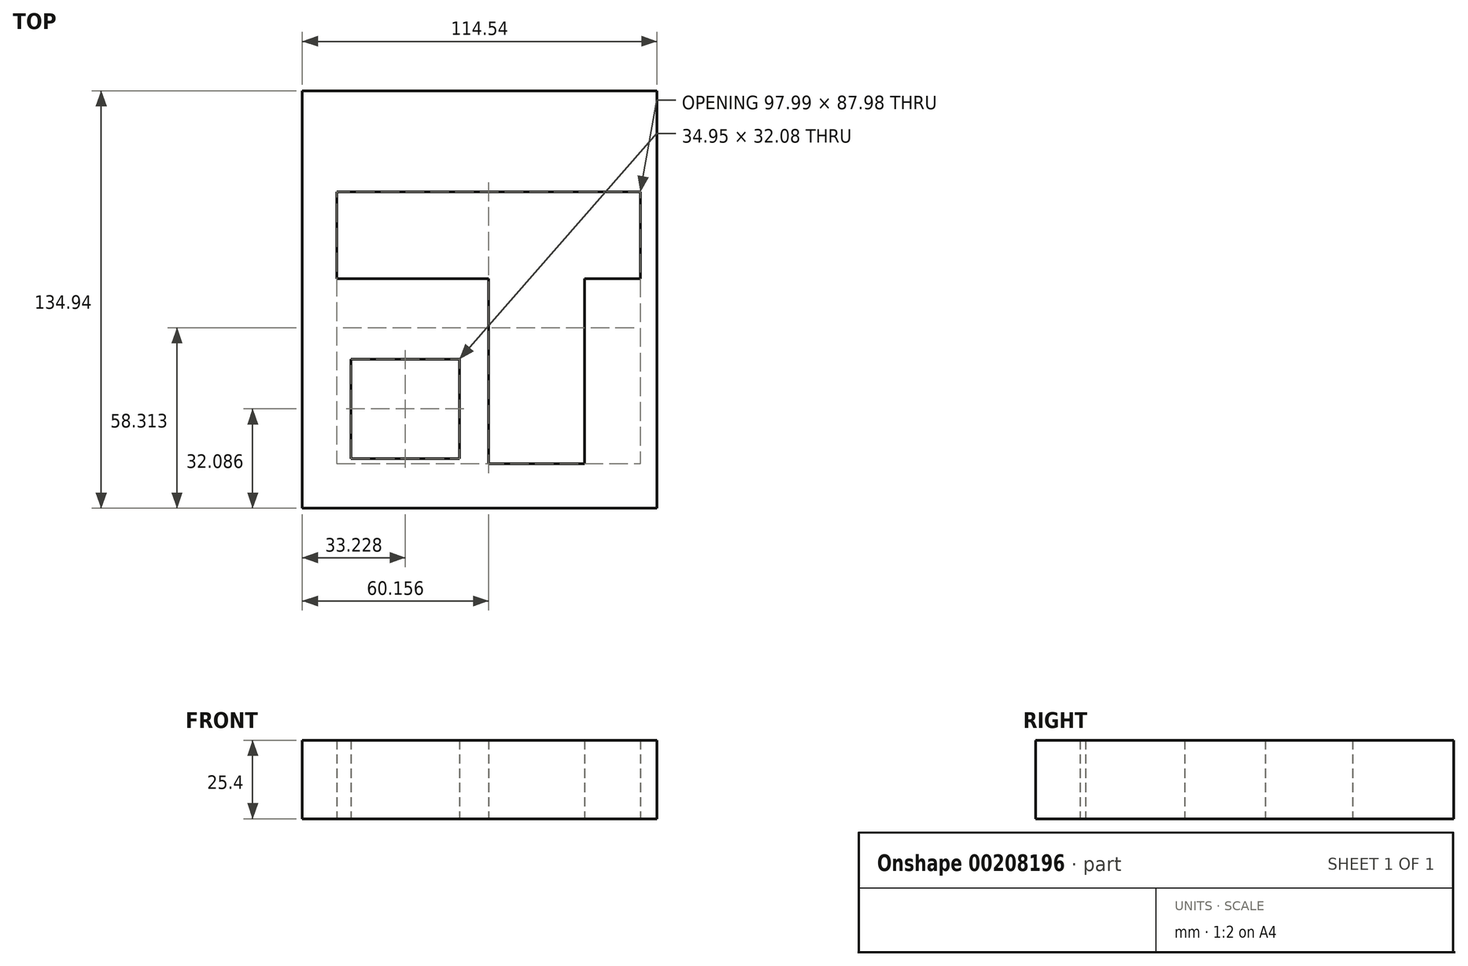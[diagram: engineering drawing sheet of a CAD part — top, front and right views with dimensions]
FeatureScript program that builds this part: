
annotation { "Feature Type Name" : "Feature", "Feature Type Description" : "" }
export const myFeature = defineFeature(function(context is Context, id is Id, definition is map)
    precondition{}
    {
        {
            var Q0;
            Q0=qCreatedBy(makeId("Top.planeOp"),FACE);
            var sketch = newSketch(context, id + "F0", { "sketchPlane" : qUnion([Q0])});
            skLineSegment(sketch, "E0.bottom", {"start": v(-57.27, -67.47) * mm, "end": v(57.27, -67.47) * mm});
            skLineSegment(sketch, "E0.top", {"start": v(-57.27, 67.47) * mm, "end": v(57.27, 67.47) * mm});
            skLineSegment(sketch, "E0.left", {"start": v(-57.27, -67.47) * mm, "end": v(-57.27, 67.47) * mm});
            skLineSegment(sketch, "E0.right", {"start": v(57.27, -67.47) * mm, "end": v(57.27, 67.47) * mm});
            skPoint(sketch, "E0.middle", {"position": v(0, 0) * mm});
            skLineSegment(sketch, "E1.bottom", {"start": v(-41.52, -51.43) * mm, "end": v(-6.57, -51.43) * mm});
            skLineSegment(sketch, "E1.top", {"start": v(-41.52, -19.34) * mm, "end": v(-6.57, -19.34) * mm});
            skLineSegment(sketch, "E1.left", {"start": v(-41.52, -51.43) * mm, "end": v(-41.52, -19.34) * mm});
            skLineSegment(sketch, "E1.right", {"start": v(-6.57, -51.43) * mm, "end": v(-6.57, -19.34) * mm});
            skPoint(sketch, "E1.middle", {"position": v(-24.04, -35.38) * mm});
            skLineSegment(sketch, "E2.bottom", {"start": v(2.89, -53.15) * mm, "end": v(33.82, -53.15) * mm});
            skLineSegment(sketch, "E2.top", {"start": v(2.89, 20.76) * mm, "end": v(33.82, 20.76) * mm});
            skLineSegment(sketch, "E2.left", {"start": v(2.89, -53.15) * mm, "end": v(2.89, 20.76) * mm});
            skLineSegment(sketch, "E2.right", {"start": v(33.82, -53.15) * mm, "end": v(33.82, 20.76) * mm});
            skPoint(sketch, "E2.middle", {"position": v(18.36, -16.2) * mm});
            skLineSegment(sketch, "E3.bottom", {"start": v(51.88, 34.83) * mm, "end": v(-46.11, 34.83) * mm});
            skLineSegment(sketch, "E3.top", {"start": v(51.88, 6.7) * mm, "end": v(-46.11, 6.7) * mm});
            skLineSegment(sketch, "E3.left", {"start": v(51.88, 34.83) * mm, "end": v(51.88, 6.7) * mm});
            skLineSegment(sketch, "E3.right", {"start": v(-46.11, 34.83) * mm, "end": v(-46.11, 6.7) * mm});
            skPoint(sketch, "E3.middle", {"position": v(2.89, 20.76) * mm});
            skSolve(sketch);
        }
        {
            var Q0;
            Q0 = qSketchRegion(id + "F0", true);
            extrude(context, id + "F1", {"entities" : qUnion([Q0]), "depth" : 25.4 * mm});
        }
    });
